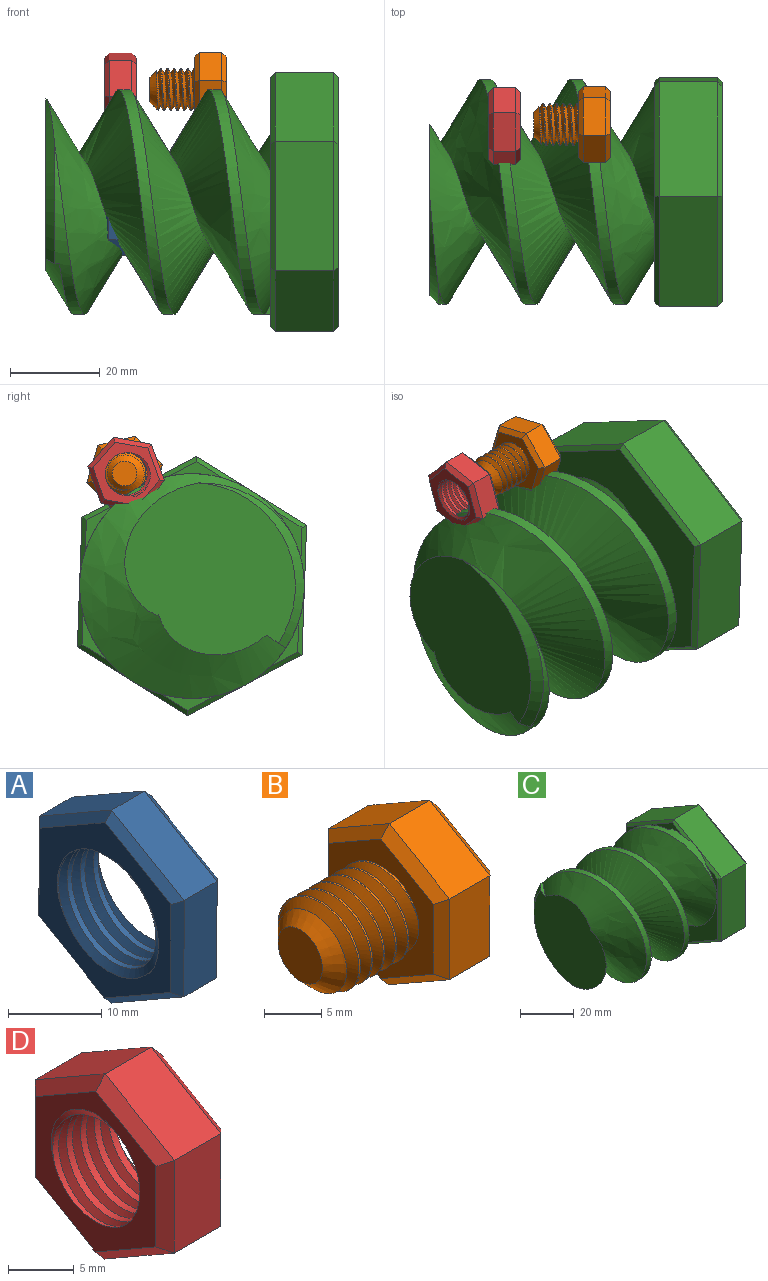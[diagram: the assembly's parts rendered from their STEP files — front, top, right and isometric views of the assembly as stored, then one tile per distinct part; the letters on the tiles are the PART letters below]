
ASSEMBLY  parts=4 mates=2
PART A: 23 faces, bbox 9.3x22.7x26 mm
  f0: cylinder r=7.24mm len=14.48mm, axis (1,0,0), area 111.6mm2, adj f7,f8,f21,f22
  f1: plane 10.98x6.38mm, normal (0,-0.5,0.86), area 63.5mm2, adj f2,f6,f14,f18
  f2: plane 12.7x5mm, normal (0,-1,0), area 63.5mm2, adj f1,f3,f12,f16
  f3: plane 11.02x6.32mm, normal (0,-0.5,-0.87), area 63.5mm2, adj f2,f4,f10,f15
  f4: plane 10.98x6.38mm, normal (0,0.5,-0.86), area 63.5mm2, adj f3,f5,f9,f17
  f5: plane 12.7x5mm, normal (0,1,0), area 63.5mm2, adj f4,f6,f11,f19
  f6: plane 11.02x6.32mm, normal (0,0.5,0.87), area 63.5mm2, adj f1,f5,f13,f20
  f7: plane 23.73x20.67mm, normal (-1,0,0), area 164.4mm2, adj f0,f9,f10,f11,f12,f13,f14,f21
  f8: plane 23.73x20.67mm, normal (1,0,0), area 164.4mm2, adj f0,f15,f16,f17,f18,f19,f20,f21
  f9: plane 10.99x6.96mm, normal (-0.71,0.36,-0.61), area 17.1mm2, adj f4,f7,f10,f11
  f10: plane 11.02x6.9mm, normal (-0.71,-0.35,-0.61), area 17.1mm2, adj f3,f7,f9,f12
  f11: plane 12.7x1.03mm, normal (-0.71,0.71,0), area 17.1mm2, adj f5,f7,f9,f13
  f12: plane 12.7x1.03mm, normal (-0.71,-0.71,0), area 17.1mm2, adj f2,f7,f10,f14
  f13: plane 11.02x6.9mm, normal (-0.71,0.35,0.61), area 17.1mm2, adj f6,f7,f11,f14
  f14: plane 10.99x6.96mm, normal (-0.71,-0.36,0.61), area 17.1mm2, adj f1,f7,f12,f13
  f15: plane 11.02x6.9mm, normal (0.71,-0.35,-0.61), area 17.1mm2, adj f3,f8,f16,f17
  f16: plane 12.7x1.03mm, normal (0.71,-0.71,0), area 17.1mm2, adj f2,f8,f15,f18
  f17: plane 10.99x6.96mm, normal (0.71,0.36,-0.61), area 17.1mm2, adj f4,f8,f15,f19
  f18: plane 10.99x6.96mm, normal (0.71,-0.36,0.61), area 17.1mm2, adj f1,f8,f16,f20
  f19: plane 12.7x1.03mm, normal (0.71,0.71,0), area 17.1mm2, adj f5,f8,f17,f20
  f20: plane 11.02x6.9mm, normal (0.71,0.35,0.61), area 17.1mm2, adj f6,f8,f18,f19
  f21: bspline ~19.31x16.73mm, area 223mm2, adj f0,f7,f8,f22
  f22: bspline ~19.31x16.73mm, area 223mm2, adj f0,f7,f8,f21
PART B: 25 faces, bbox 17.8x15.9x18.1 mm
  f0: cylinder r=4.75mm len=9.5mm, axis (1,0,0), area 28.1mm2, adj f1,f2,f4,f12
  f1: bspline ~10.97x9.91mm, area 196.7mm2, adj f0,f2,f4,f12
  f2: bspline ~10.97x10.66mm, area 196.6mm2, adj f0,f1,f4,f12
  f3: plane 5.5x5.5mm, normal (-1,0,0), area 23.8mm2, adj f4
  f4: cone r=4.75mm half-angle=45deg, axis (1,0,0), area 47.4mm2, adj f0,f1,f2,f3
  f5: plane 7.48x5mm, normal (0,-0.5,0.86), area 43.3mm2, adj f6,f10,f18,f22
  f6: plane 8.66x5mm, normal (0,-1,0), area 43.3mm2, adj f5,f7,f16,f20
  f7: plane 7.52x5mm, normal (0,-0.5,-0.87), area 43.3mm2, adj f6,f8,f14,f19
  f8: plane 7.48x5mm, normal (0,0.5,-0.86), area 43.3mm2, adj f7,f9,f13,f21
  f9: plane 8.66x5mm, normal (0,1,0), area 43.3mm2, adj f8,f10,f15,f23
  f10: plane 7.52x5mm, normal (0,0.5,0.87), area 43.3mm2, adj f5,f9,f17,f24
  f11: plane 15.01x13.03mm, normal (1,0,0), area 146.4mm2, adj f13,f14,f15,f16,f17,f18
  f12: plane 15.83x13.85mm, normal (-1,0,0), area 89.2mm2, adj f0,f1,f2,f19,f20,f21,f22,f23
  f13: plane 7.49x4.93mm, normal (0.71,0.36,-0.61), area 11.4mm2, adj f8,f11,f14,f15
  f14: plane 7.52x4.88mm, normal (0.71,-0.35,-0.61), area 11.4mm2, adj f7,f11,f13,f16
  f15: plane 8.66x1.03mm, normal (0.71,0.71,0), area 11.4mm2, adj f9,f11,f13,f17
  f16: plane 8.66x1.03mm, normal (0.71,-0.71,0), area 11.4mm2, adj f6,f11,f14,f18
  f17: plane 7.52x4.88mm, normal (0.71,0.35,0.61), area 11.4mm2, adj f10,f11,f15,f18
  f18: plane 7.49x4.93mm, normal (0.71,-0.36,0.61), area 11.4mm2, adj f5,f11,f16,f17
  f19: plane 7.52x4.88mm, normal (-0.71,-0.35,-0.61), area 11.4mm2, adj f7,f12,f20,f21
  f20: plane 8.66x1.03mm, normal (-0.71,-0.71,0), area 11.4mm2, adj f6,f12,f19,f22
  f21: plane 7.49x4.93mm, normal (-0.71,0.36,-0.61), area 11.4mm2, adj f8,f12,f19,f23
  f22: plane 7.49x4.93mm, normal (-0.71,-0.36,0.61), area 11.4mm2, adj f5,f12,f20,f24
  f23: plane 8.66x1.03mm, normal (-0.71,0.71,0), area 11.4mm2, adj f9,f12,f21,f24
  f24: plane 7.52x4.88mm, normal (-0.71,0.35,0.61), area 11.4mm2, adj f10,f12,f22,f23
PART C: 27 faces, bbox 78.5x56.8x62 mm
  f0: cylinder r=25mm len=50mm, axis (1,0,0), area 978.1mm2, adj f1,f2,f3,f5,f6,f14,f24
  f1: bspline ~66.75x52.57mm, area 4786.1mm2, adj f0,f2,f4,f6,f14
  f2: bspline ~66.75x52.57mm, area 4822.3mm2, adj f0,f1,f3,f4,f5,f14
  f3: plane 2.17x1.25mm, normal (0,1,0), area 1.4mm2, adj f0,f2,f14
  f4: plane 42.39x42.39mm, normal (-1,0,0), area 1097.9mm2, adj f1,f2,f5,f6
  f5: cone r=25mm half-angle=45deg, axis (1,0,0), area 107.8mm2, adj f0,f2,f4,f6
  f6: plane 4.43x3.01mm, normal (0,-0.52,0.85), area 5.8mm2, adj f0,f1,f4,f5
  f7: plane 24.98x14.47mm, normal (0,-0.5,0.87), area 375.3mm2, adj f8,f12,f20,f24
  f8: plane 28.87x13mm, normal (0,-1,0), area 375.3mm2, adj f7,f9,f18,f22
  f9: plane 25.02x14.4mm, normal (0,-0.5,-0.87), area 375.3mm2, adj f8,f10,f16,f21
  f10: plane 24.98x14.47mm, normal (0,0.5,-0.87), area 375.3mm2, adj f9,f11,f15,f23
  f11: plane 28.87x13mm, normal (0,1,0), area 375.3mm2, adj f10,f12,f17,f25
  f12: plane 25.02x14.4mm, normal (0,0.5,0.87), area 375.3mm2, adj f7,f11,f19,f26
  f13: plane 55.43x48.04mm, normal (1,0,0), area 1995.3mm2, adj f15,f16,f17,f18,f19,f20
  f14: plane 55.43x48.04mm, normal (-1,0,0), area 861.9mm2, adj f0,f1,f2,f3,f21,f22,f23,f24
  f15: plane 24.98x15.05mm, normal (0.71,0.35,-0.61), area 40mm2, adj f10,f13,f16,f17
  f16: plane 25.02x14.98mm, normal (0.71,-0.35,-0.61), area 40mm2, adj f9,f13,f15,f18
  f17: plane 28.87x1.04mm, normal (0.71,0.71,0), area 40mm2, adj f11,f13,f15,f19
  f18: plane 28.87x1.04mm, normal (0.71,-0.71,0), area 40mm2, adj f8,f13,f16,f20
  f19: plane 25.02x14.98mm, normal (0.71,0.35,0.61), area 40mm2, adj f12,f13,f17,f20
  f20: plane 24.98x15.05mm, normal (0.71,-0.35,0.61), area 40mm2, adj f7,f13,f18,f19
  f21: plane 25.02x14.98mm, normal (-0.71,-0.35,-0.61), area 40mm2, adj f9,f14,f22,f23
  f22: plane 28.87x1.04mm, normal (-0.71,-0.71,0), area 40mm2, adj f8,f14,f21,f24
  f23: plane 24.98x15.05mm, normal (-0.71,0.35,-0.61), area 40mm2, adj f10,f14,f21,f25
  f24: plane 24.98x15.05mm, normal (-0.71,-0.35,0.61), area 26.8mm2, adj f0,f7,f14,f22,f26
  f25: plane 28.87x1.04mm, normal (-0.71,0.71,0), area 40mm2, adj f11,f14,f23,f26
  f26: plane 25.02x14.98mm, normal (-0.71,0.35,0.61), area 40mm2, adj f12,f14,f24,f25
PART D: 23 faces, bbox 9.1x15.4x17.7 mm
  f0: plane 7.49x5mm, normal (0,-0.5,0.86), area 43.3mm2, adj f1,f5,f13,f17
  f1: plane 8.66x5mm, normal (0,-1,0), area 43.3mm2, adj f0,f2,f11,f15
  f2: plane 7.51x5mm, normal (0,-0.5,-0.87), area 43.3mm2, adj f1,f3,f9,f14
  f3: plane 7.49x5mm, normal (0,0.5,-0.86), area 43.3mm2, adj f2,f4,f8,f16
  f4: plane 8.66x5mm, normal (0,1,0), area 43.3mm2, adj f3,f5,f10,f18
  f5: plane 7.51x5mm, normal (0,0.5,0.87), area 43.3mm2, adj f0,f4,f12,f19
  f6: plane 15.37x13.38mm, normal (-1,0,0), area 71.4mm2, adj f8,f9,f10,f11,f12,f13,f20,f21
  f7: plane 15.37x13.38mm, normal (1,0,0), area 71.4mm2, adj f14,f15,f16,f17,f18,f19,f20,f21
  f8: plane 7.49x4.93mm, normal (-0.71,0.36,-0.61), area 11.4mm2, adj f3,f6,f9,f10
  f9: plane 7.51x4.89mm, normal (-0.71,-0.35,-0.61), area 11.4mm2, adj f2,f6,f8,f11
  f10: plane 8.66x1.02mm, normal (-0.71,0.71,0), area 11.4mm2, adj f4,f6,f8,f12
  f11: plane 8.66x1.02mm, normal (-0.71,-0.71,0), area 11.4mm2, adj f1,f6,f9,f13
  f12: plane 7.51x4.89mm, normal (-0.71,0.35,0.61), area 11.4mm2, adj f5,f6,f10,f13
  f13: plane 7.49x4.93mm, normal (-0.71,-0.36,0.61), area 11.4mm2, adj f0,f6,f11,f12
  f14: plane 7.51x4.89mm, normal (0.71,-0.35,-0.61), area 11.4mm2, adj f2,f7,f15,f16
  f15: plane 8.66x1.02mm, normal (0.71,-0.71,0), area 11.4mm2, adj f1,f7,f14,f17
  f16: plane 7.49x4.93mm, normal (0.71,0.36,-0.61), area 11.4mm2, adj f3,f7,f14,f18
  f17: plane 7.49x4.93mm, normal (0.71,-0.36,0.61), area 11.4mm2, adj f0,f7,f15,f19
  f18: plane 8.66x1.02mm, normal (0.71,0.71,0), area 11.4mm2, adj f4,f7,f16,f19
  f19: plane 7.51x4.89mm, normal (0.71,0.35,0.61), area 11.4mm2, adj f5,f7,f17,f18
  f20: cylinder r=4.66mm len=9.32mm, axis (1,0,0), area 85.4mm2, adj f6,f7,f21,f22
  f21: bspline ~12.5x10.82mm, area 128.4mm2, adj f6,f7,f20,f22
  f22: bspline ~12.5x10.82mm, area 128.5mm2, adj f6,f7,f20,f21
PLACE A rot(axis=(0,0.6,-0.8),180deg) t=(-55.27,-6.86,23.48)mm fixed
PLACE B rot(axis=(-1,0,0),43.8deg) t=(-31.66,7.73,48.08)mm
PLACE C rot(axis=(-1,0,0),178.1deg) t=(-10.77,-7.25,23.06)mm
PLACE D rot(axis=(1,0,0),100.2deg) t=(-48.16,7.38,48.02)mm fixed
MATE cylindrical C.f0 <-> A.f7  axis (-1,0,0) through (-68.27,-7.25,23.06)mm
MATE cylindrical B.f0 <-> D.f6  axis (-1,0,0) through (-45.16,7.73,48.08)mm
